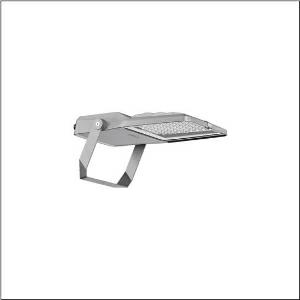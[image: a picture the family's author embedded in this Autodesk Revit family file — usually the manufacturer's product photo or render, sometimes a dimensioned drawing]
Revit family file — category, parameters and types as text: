
# Revit family: floodlight_fl_21_mini___pl33t_5xa7776d2f1a_88fb
name_source: partatom
category: Lighting Fixtures
units: mm (PartAtom-declared; Revit-internal decimal feet)

## family parameters
Cut with Voids When Loaded = No
Host = Face
Light Source = No
Part Type = Normal
Room Calculation Point = No
Round Connector Dimension = Use Diameter
Shared = No

## types (1)
- --- (1 x LED, 17630 lm, 142.9 W, 3000K)
    Apparent Load = 143 VA
    CIE Flux Codes = 26 75 99 100 100
    Color Rendering = 70
    Color Temperature = 3000K
    Default Elevation = 1800 mm
    Description = Floodlight FL 21 mini, floodlight, primary light control with lens, of PMMA, primary optical cover: protective disc, of toughened safety glass, transparent, light distribution: PL33T, light emission: direct distribution, installation type: surface-mounted, LED, High Power LED, rated luminous flux: 17.630lm, luminous efficacy: 123lm/W, light colour: 730, colour temperature: 3000K, control gear: Smart Interface (Zhaga), control: flexible luminous flux parameterisation, time-dependent luminous flux control, constant luminous flux control, overheat protection, pre-setting: logarithmic dimming characteristic, with terminal, 6-pole, mains connection: 220..240V, AC, 50/60Hz, start of lifetime: 143W, end of service life: 151W, reduction: 63W, luminaire housing, of diecast aluminium, powder-coated, Siteco® metallic grey (DB 702S), corrosivity category C5 mid according to DIN EN ISO 12944, suitable for swimming pools, chlorine-resistant, sealing non-destructively replaceable, mounting bracket, of steel, galvanised, powder-coated, Siteco® metallic grey (DB 702S), Smart Interface below and above, protection rating (complete): IP66, insulation class (complete): insulation class II (safety insulation), certification: CE, ENEC, VDE, protection symbol: D, impact resistance: IK08, permissible operating ambient temperature: -40..+40°C, permissible operating ambient temperature for outdoor applications: -40..+50°C, standard: DIN EN 12944, LABS conformity tested according to VDMA 24364:2018-05, packaging unit: 1 piece

Light Distribution: PL33T
    Height = 70 mm
    Lamp = 1 x LED
    Lamp Light Flux = 17630 lm
    Lamp Power = 142.9 W
    Lamp count = 1
    Length = 485 mm
    Luminous efficacy = 123 lm/W
    Manufacturer = Siteco
    ModVariant = No
    Model = 5XA7776D2F1A
    Number of Poles = 1
    OnlyDefault = Yes
    Power Factor = 1
    Product Name = Floodlight FL 21 mini | PL33T
    Product group = floodlight | pylon annexe
    ProductGroupID = 6201
    Protection Class = Protection class II
    Protection Degree = IP 66
    RLX_Detail_Level = 1
    RLX_Emergency_Light_Flux = 0 lm
    RLX_Emergency_Type = 0
    RLX_Emergency_Type_DB = No
    RlxData = <blob elided: 96281 chars, md5=de5060ac>
    Socket = socket
    Standby Power = 0 W
    System Light Flux = 17630 lm
    System Power = 143 W
    Type Comments = factory setting: luminous flux: 100 % | dim-lin: 254 | 730 mA
    Type Image = l_1006845.jpg
    URL = http://relux.com
    VarID = @adj_169803
    Voltage = 0 V
    Weight = 0.00 kg
    Width = 337 mm

## geometry (parser evidence)
native form markers: Blend x4, Sweep x14
no freeform markers — native parametric forms only
